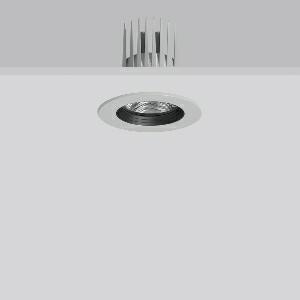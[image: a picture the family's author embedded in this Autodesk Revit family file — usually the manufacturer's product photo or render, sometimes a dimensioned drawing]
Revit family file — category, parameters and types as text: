
# Revit family: heledon_mini_e_901741_004_76_e1fa
name_source: partatom
category: Lighting Fixtures
units: mm (PartAtom-declared; Revit-internal decimal feet)

## family parameters
Cut with Voids When Loaded = No
Host = Face
Light Source = No
Part Type = Normal
Room Calculation Point = No
Round Connector Dimension = Use Diameter
Shared = No

## types (1)
- HELEDON mini E (1 x LED Modul 930, 2450 lm, 3000)
    Apparent Load = 20 VA
    Approval mark = CE
    CIE Flux Codes = 99 100 100 100 100
    Color Rendering = 90
    Color Temperature = 3000
    Default Elevation = 1800 mm
    Description = Series: HELEDON mini
Round recessed downlight. Housing: die-cast aluminium, powder-coated. Black plastic ring and recessed LED to prevent glare from the side. Optical assembly with reflector made of MIRO-Silver with 98% total light reflection for outstanding efficiency - can be changed without tools. Best colour rendering index Ra>90. Suitable for Recessed ceiling mounting. Installation without tools thanks to spring fastening system. Including separate LED converter with connecting cable 600 mm.High quality converter without flickering and stroboscopic effect. Through-wiring box (5 pole) available as accessory. The following accessories can be mounted without use of tools: interchangeable lenses, decorative glasses, honeycomb louvre, clear and frosted diffusers, white interchangeable plastic ring. 
Colour: silver
Diameter: 124 mm
Height: 3 mm
Cut-out diameter: 114 mm
Recess height: 170 mm
Luminaire: recess height: 120 mm
Lamp: LED
Socket: without socket
Colour temperature: 3000K
Colour rendering index (CRI): 92
System power: 20 W
Rated luminous flux: 2450 lm
Luminous efficiency: 123 lm/W
Control gear: Converter, dimmable, DALI
Protection class: II
Type of protection: IP 20
    Height = 0 mm  [stored 0 ft]
    Lamp = 1 x LED Modul 930
    Lamp Light Flux = 2450 lm
    Lamp count = 1
    Length = 124 mm  [stored 0.406824 ft]
    Lifetime = 50000 h
    Luminous efficacy = 123 lm/W
    Manufacturer = RZB
    ModVariant = No
    Model = 901741.004.76
    Mounting Place = Ceiling
    Mounting Type = Recessed
    Number of Poles = 1
    OnlyDefault = Yes
    Power Factor = 1
    Product Name = HELEDON mini E
    Product group = Recessed downlights
    ProductGroupID = 402
    Protection Class = Protection class II
    Protection Degree = IP 20
    RLX_Detail_Level = 1
    RLX_Emergency_Light_Flux = 0 lm
    RLX_Emergency_Type = 0
    RLX_Emergency_Type_DB = No
    RlxData = <blob elided: 125945 chars, md5=93b02cca>
    Socket = socket
    Standby Power = 0 W
    System Light Flux = 2450 lm
    System Power = 20 W
    Type Comments = Product without accessories
    Type Image = 901657.004.jpg
    URL = http://relux.com
    VarID = ---
    Voltage = 230 V
    Voltage Range = 220-240 V
    Weight = 0.00 kg
    Width = 0 mm  [stored 0 ft]

note: [stored X ft] marks values corroborated as IEEE doubles in the binary element streams (Revit-internal decimal feet)

## geometry (parser evidence)
native form markers: Blend x4, Sweep x9
no freeform markers — native parametric forms only
